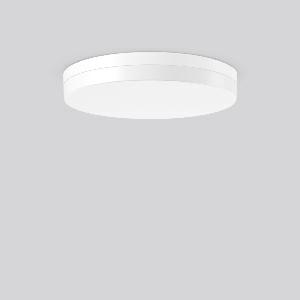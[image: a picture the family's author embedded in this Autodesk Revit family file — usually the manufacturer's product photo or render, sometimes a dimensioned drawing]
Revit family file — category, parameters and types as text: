
# Revit family: flat_slim_round_312633_002_4a3a
name_source: partatom
category: Lighting Fixtures
units: mm (PartAtom-declared; Revit-internal decimal feet)

## family parameters
Cut with Voids When Loaded = No
Host = Face
Light Source = No
Part Type = Normal
Room Calculation Point = No
Round Connector Dimension = Use Diameter
Shared = No

## types (1)
- MultiLumen 1 830 (1 x LED Modul 830, 3350 lm, 3000)
    Apparent Load = 31 VA
    CIE Flux Codes = 41 71 90 86 100
    Color Rendering = 80
    Color Temperature = 3000
    Default Elevation = 1800 mm
    Height = 75 mm
    Lamp = 1 x LED Modul 830
    Lamp Light Flux = 3350 lm
    Lamp count = 1
    Length = 480 mm
    Lifetime = 50000 h
    Luminous efficacy = 108 lm/W
    Manufacturer = RZB
    ModVariant = No
    Model = 312633.002
    Mounting Place = Ceiling
    Mounting Type = Surface mounted
    Number of Poles = 1
    OnlyDefault = Yes
    Power Factor = 1
    Product Name = FLAT SLIM round
    Product group = Surface mounted ceiling and wall luminaires
    ProductGroupID = 305
    Protection Class = Protection class I
    Protection Degree = Degree of protection
    RLX_Detail_Level = 1
    RLX_Emergency_Light_Flux = 0 lm
    RLX_Emergency_Type = 0
    RLX_Emergency_Type_DB = No
    RlxData = <blob elided: 21033 chars, md5=9e45dc2d>
    Socket = socket
    Standby Power = 0 W
    System Light Flux = 3350 lm
    System Power = 31 W
    Type Comments = MultiLumen 1 830
    Type Image = 312633.002.jpg
    URL = http://relux.com
    VarID = multilumen_1_830
    Voltage = 0 V
    Weight = 0.00 kg
    Width = 0 mm  [stored 0 ft]

note: [stored X ft] marks values corroborated as IEEE doubles in the binary element streams (Revit-internal decimal feet)

## geometry (parser evidence)
native form markers: Blend x4, Sweep x13
no freeform markers — native parametric forms only
